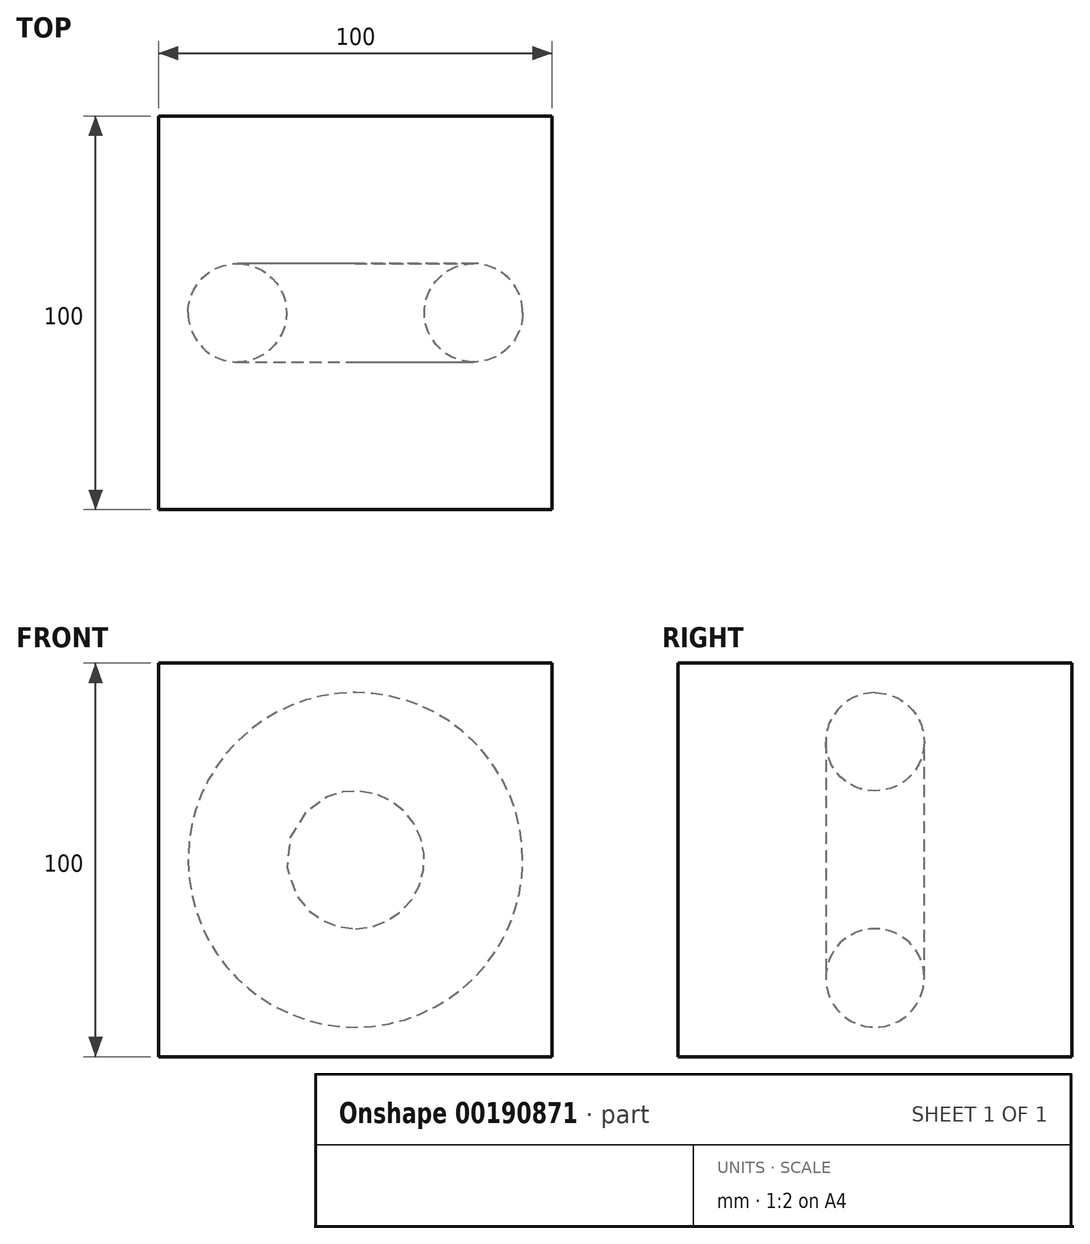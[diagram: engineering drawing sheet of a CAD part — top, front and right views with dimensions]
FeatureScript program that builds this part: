
annotation { "Feature Type Name" : "Feature", "Feature Type Description" : "" }
export const myFeature = defineFeature(function(context is Context, id is Id, definition is map)
    precondition{}
    {
        {
            var Q0;
            Q0=qCreatedBy(makeId("Front.planeOp"),FACE);
            var sketch = newSketch(context, id + "F0", { "sketchPlane" : qUnion([Q0])});
            skLineSegment(sketch, "E0.bottom", {"start": v(50, 50) * mm, "end": v(-50, 50) * mm});
            skLineSegment(sketch, "E0.top", {"start": v(50, -50) * mm, "end": v(-50, -50) * mm});
            skLineSegment(sketch, "E0.left", {"start": v(50, 50) * mm, "end": v(50, -50) * mm});
            skLineSegment(sketch, "E0.right", {"start": v(-50, 50) * mm, "end": v(-50, -50) * mm});
            skPoint(sketch, "E0.middle", {"position": v(0, 0) * mm});
            skSolve(sketch);
        }
        {
            var Q0;
            Q0 = qSketchRegion(id + "F0", true);
            extrude(context, id + "F1", {"entities" : qUnion([Q0]), "depth" : 100 * mm, "symmetric" : true});
        }
        {
            var Q0;
            Q0=qCreatedBy(makeId("Right.planeOp"),FACE);
            var sketch = newSketch(context, id + "F2", { "sketchPlane" : qUnion([Q0])});
            skCircle(sketch, "E1", {"center": v(0, 30) * mm, "radius": 12.5 * mm});
            skLineSegment(sketch, "E2", {"start": v(-26.72, 0) * mm, "end": v(34.63, 0) * mm, "construction": true});
            skSolve(sketch);
        }
        {
            var Q0;
            Q0 = qSketchRegion(id + "F2", true);
            var Q1;
            Q1=sQuery(id+"F2.wireOp",EDGE,"E2");
            revolve(context, id + "F3", {"entities" : qUnion([Q0]), "axis" : qUnion([Q1]), "revolveType" : RevolveType.FULL});
        }
    });
